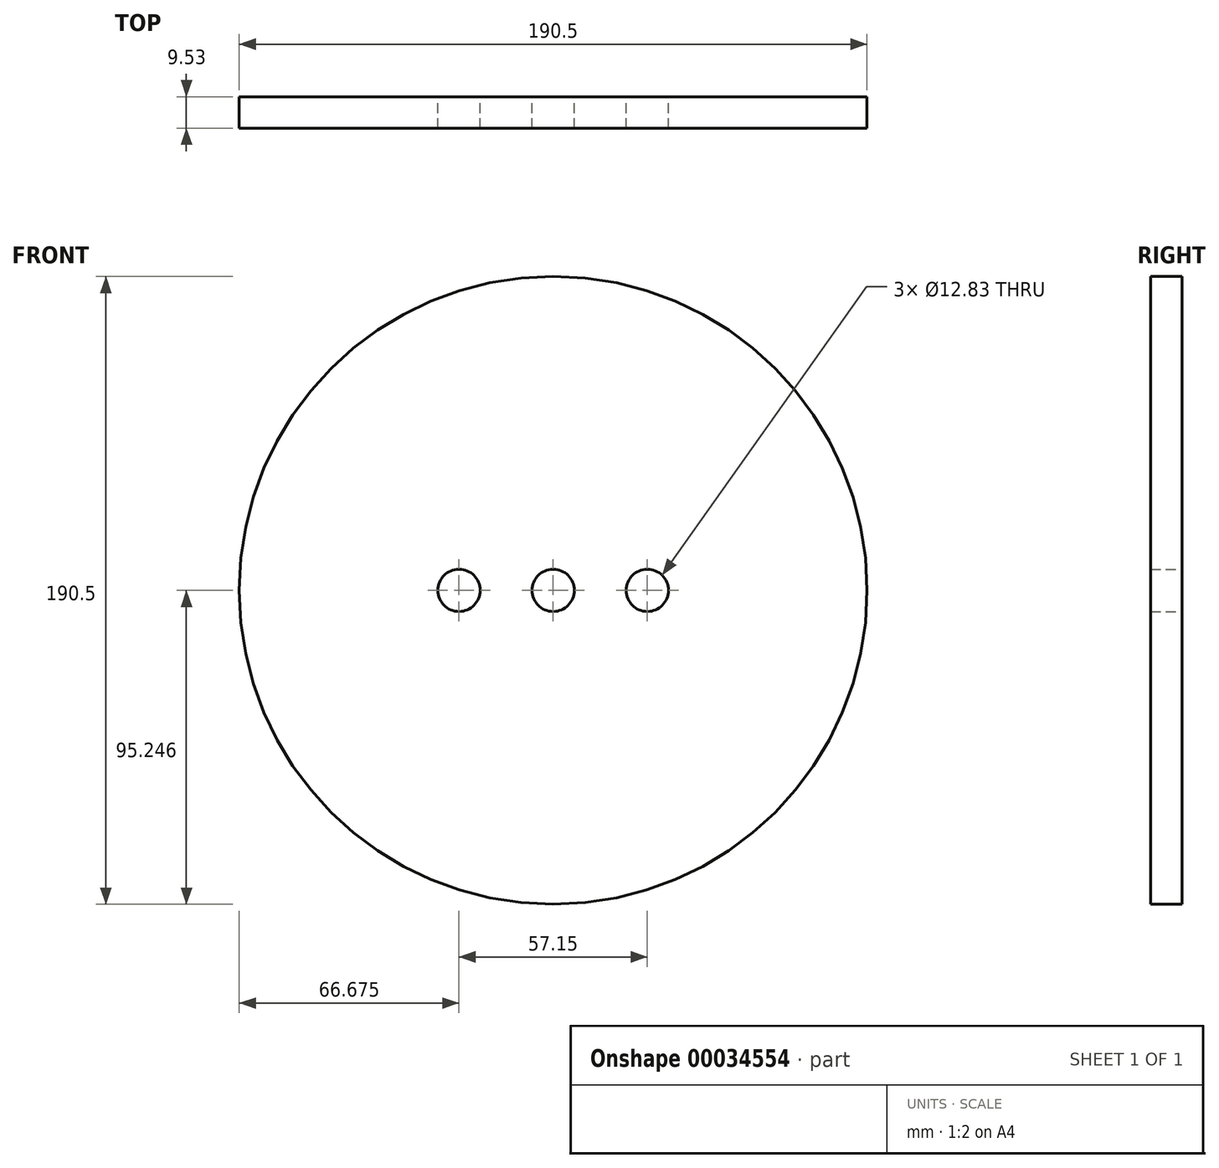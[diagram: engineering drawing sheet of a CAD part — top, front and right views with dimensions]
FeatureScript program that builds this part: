
annotation { "Feature Type Name" : "Feature", "Feature Type Description" : "" }
export const myFeature = defineFeature(function(context is Context, id is Id, definition is map)
    precondition{}
    {
        {
            var Q0;
            Q0=qCreatedBy(makeId("Front.planeOp"),FACE);
            var sketch = newSketch(context, id + "F0", { "sketchPlane" : qUnion([Q0])});
            skCircle(sketch, "E0", {"center": v(-27.89, 17.47) * mm, "radius": 95.25 * mm});
            skCircle(sketch, "E1", {"center": v(-27.89, 17.47) * mm, "radius": 6.41 * mm});
            skLineSegment(sketch, "E2", {"start": v(-123.14, 17.47) * mm, "end": v(67.36, 17.47) * mm, "construction": true});
            skCircle(sketch, "E3", {"center": v(-56.46, 17.47) * mm, "radius": 6.41 * mm});
            skCircle(sketch, "E4", {"center": v(0.69, 17.47) * mm, "radius": 6.41 * mm});
            skSolve(sketch);
        }
        {
            var Q0;
            Q0=makeQuery(id+"F0.imprint","IMPRINT",FACE,{"disambiguationData":[TD([[makeQuery(id+"F0.imprint","IMPRINT",EDGE,{"derivedFrom":sQuery(id+"F0.wireOp",EDGE,"E0")}),1.0]])]});
            extrude(context, id + "F1", {"entities" : qUnion([Q0]), "depth" : 9.52 * mm});
        }
    });
